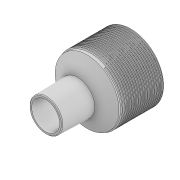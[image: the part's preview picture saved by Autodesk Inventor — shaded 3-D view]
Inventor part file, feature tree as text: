
AUTODESK INVENTOR PART (.ipt)
format: ipt  version: 2020 (Build 240168000, 168)  size: 891,904 bytes
history: native  units: mm
features: sketch x16, extrude x9, chamfer x8, revolve x5, helix x2, plane x2, split x1, projected_geometry x1
ambient origin geometry x8: Origin, YZ Plane, XZ Plane, XY Plane, X Axis, Y Axis, Z Axis, Center Point
bodies: Solid1 (feature_tree)
feature tree (44):
  extrude  "Extrusion1"  Depth=2.0mm
  chamfer  "Chamfer1"  Distance=2.0mm
  revolve  "Revolution1"  [1 undecoded]
  extrude  "Extrusion2"  Depth=18.75mm
  sketch  "Sketch6"  dims[d17=1.6mm]
  helix  "Coil2"  [1 undecoded]
  chamfer  "Chamfer4"  Distance=10.0mm
  chamfer  "Chamfer5"  Distance=0.65mm Angle=45.0deg
  extrude  "Extrusion4"  Depth=42.0mm
  extrude  "Extrusion6"  Depth=2.65mm
  extrude  "Extrusion7"  Depth=1.2mm
  helix  "Coil3"  [1 undecoded]
  extrude  "Extrusion8"  Depth=10.0mm TaperAngle=0.0deg
  revolve  "Revolution2"  [1 undecoded]
  extrude  "Extrusion9"  Depth=10.0mm
  plane  "Work Plane3"
  split  "Split2"
  revolve  "Revolution3"  [1 undecoded]
  sketch  "Sketch17"  dims[d54=0.65mm d55=4.0mm d56=45.0deg d57=42.0mm]
  revolve  "Revolution6"  [1 undecoded]
  plane  "Work Plane4"
  extrude  "Extrusion10"  Depth=10.0mm TaperAngle=0.0deg
  chamfer  "Chamfer9"  Angle=135.0deg  [1 undecoded]
  chamfer  "Chamfer10"  Angle=90.0deg  [1 undecoded]
  revolve  "Revolution8"  [1 undecoded]
  chamfer  "Chamfer12"  [1 undecoded]
  chamfer  "Chamfer13"  Distance=21.0mm
  extrude  "Extrusion11"  Depth=10.0mm
  chamfer  "Chamfer14"  Distance=1.6mm
  sketch  "Sketch1"  dims[d0=18.0mm d1=2.0mm d2=2.0mm d3=0.0mm]
  sketch  "Sketch4"  dims[d4=2.0mm d5=2.0mm d6=45.0deg d10=12.25mm]
  sketch  "Sketch5"  dims[d11=8.0mm d12=18.75mm d14=1.5mm]
  projected_geometry  "Projected Loop1"
  sketch  "Sketch8"  dims[d18=90.0deg d19=10.0mm d20=0.0mm]
  sketch  "Sketch9"  dims[d21=1.0mm]
  sketch  "Sketch10"  dims[d22=1.0mm]
  sketch  "Sketch11"  dims[d23=1.5mm]
  sketch  "Sketch12"  dims[d24=0.8mm]
  sketch  "Sketch13"  dims[d42=0.1mm]
  sketch  "Sketch14"  dims[d43=1.5mm]
  sketch  "Sketch15"  dims[d44=6.0mm d45=10.0mm d46=0.0mm d47=90.0deg d48=90.0deg d49=0.0mm d50=0.0mm d51=0.65mm d52=4.0mm d53=45.0deg]
  sketch  "Sketch18"  dims[d58=28.0mm d59=0.0mm d60=2.65mm]
  sketch  "Sketch19"  dims[d61=1.2mm d62=1.2mm d65=12.0mm d66=0.0mm]
  sketch  "Sketch20"  dims[d67=30.0mm d68=3.0mm d69=0.0mm d74=1.0mm d75=0.65mm d76=1.5mm d77=28.0mm d78=10.0mm d79=0.0mm d80=90.0deg d81=90.0deg d82=0.0mm d83=0.0mm d84=45.0mm d85=20.0mm d86=0.0mm d87=135.0deg d88=90.0deg d90=0.7mm d91=0.0mm d92=0.0mm d95=21.0mm d96=10.81mm d97=1.6mm d98=1.6mm d99=6.981317mm d100=90.0deg d101=0.75mm d102=1.4mm d103=18.0mm d104=2.4mm d105=2.0mm d109=15.0mm d116=90.0deg d117=45.0deg d120=10.0mm d121=2.0mm d122=12.0mm d123=0.0mm d124=0.0mm d131=0.5mm d132=2.0mm d133=45.0deg d134=17.0mm d135=13.0mm d136=3.0mm d137=2.0mm d138=45.0deg d142=90.0deg d143=1.8mm d144=2.4mm d145=45.0deg d146=2.15mm d147=2.0mm d148=45.0deg d149=0.75mm d150=0.75mm d151=8.0mm d152=10.0mm d153=0.0mm d154=15.0mm d155=2.0mm d156=45.0deg d157=15.0mm d158=11.185mm d70=0.5mm d71=0.872665mm d72=0.5mm d73=0.872665mm d89=0.5mm]
note: 10 required parameter values undecoded (feature->parameter linkage not recoverable at this tier; creation-order binding heuristic only, values carry confidence <= 0.55)